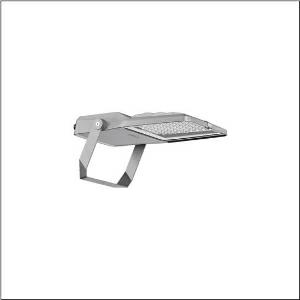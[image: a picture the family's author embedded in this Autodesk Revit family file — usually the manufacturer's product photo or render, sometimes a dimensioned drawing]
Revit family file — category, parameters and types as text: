
# Revit family: floodlight_fl_21_iq_mini___rs12_5xa7772c1b1a_888e
name_source: partatom
category: Lighting Fixtures
units: mm (PartAtom-declared; Revit-internal decimal feet)

## family parameters
Cut with Voids When Loaded = No
Host = Face
Light Source = No
Part Type = Normal
Room Calculation Point = No
Round Connector Dimension = Use Diameter
Shared = No

## types (1)
- --- (1 x LED, 10220 lm, 87.2 W, 2200K)
    Apparent Load = 87 VA
    CIE Flux Codes = 79 92 99 100 100
    Color Rendering = 70
    Color Temperature = 2200K
    Default Elevation = 1800 mm
    Description = Floodlight FL 21 iQ mini, floodlight, primary light control with lens, of PMMA, primary optical cover: protective disc, of toughened safety glass, transparent, light distribution: RS12, light emission: direct distribution, installation type: surface-mounted, LED, High Power LED, rated luminous flux: 10.220lm, luminous efficacy: 117lm/W, light colour: 722, colour temperature: 2200K, control gear: iQ Street-Remote/DALI, control: Street-Remote, Auto-Match, Temp-Guard, Night-Set, Smart-Wire, Desk-Remote (wireless, voltage-free reading and setting of iQ features in the workshop via application-optimized NFC function/RFID function), optimised constant luminous flux control (CLO 2.0), with terminal, 6-pole, mains connection: 220..240V, AC, 50/60Hz, start of lifetime: 87W, end of service life: 92W, reduction: 40W, luminaire housing, of diecast aluminium, powder-coated, Siteco® metallic grey (DB 702S), corrosivity category C5 mid according to DIN EN ISO 12944, suitable for swimming pools, chlorine-resistant, sealing non-destructively replaceable, mounting bracket, of steel, galvanised, powder-coated, Siteco® metallic grey (DB 702S), protection rating (complete): IP66, insulation class (complete): insulation class II (safety insulation), certification: CE, ENEC, VDE, protection symbol: D, impact resistance: IK08, permissible operating ambient temperature: -40..+40°C, permissible operating ambient temperature for outdoor applications: -40..+50°C, standard: DIN EN 12944, LABS conformity tested according to VDMA 24364:2018-05, packaging unit: 1 piece

Light Distribution: RS12
    Height = 70 mm
    Lamp = 1 x LED
    Lamp Light Flux = 10220 lm
    Lamp Power = 87.2 W
    Lamp count = 1
    Length = 485 mm
    Luminous efficacy = 117 lm/W
    Manufacturer = Siteco
    ModVariant = No
    Model = 5XA7772C1B1A
    Number of Poles = 1
    OnlyDefault = Yes
    Power Factor = 1
    Product Name = Floodlight FL 21 iQ mini | RS12
    Product group = floodlight | pylon annexe
    ProductGroupID = 6200
    Protection Class = Protection class II
    Protection Degree = IP 66
    RLX_Detail_Level = 1
    RLX_Emergency_Light_Flux = 0 lm
    RLX_Emergency_Type = 0
    RLX_Emergency_Type_DB = No
    RlxData = <blob elided: 91005 chars, md5=8ee5542e>
    Socket = socket
    Standby Power = 0 W
    System Light Flux = 10220 lm
    System Power = 87 W
    Type Comments = factory setting: luminous flux: 100 % | dim-lin: 254 | 456 mA
    Type Image = l_1006845.jpg
    URL = http://relux.com
    VarID = @adj_167672
    Voltage = 0 V
    Weight = 0.00 kg
    Width = 337 mm

## geometry (parser evidence)
native form markers: Blend x4, Sweep x14
no freeform markers — native parametric forms only
